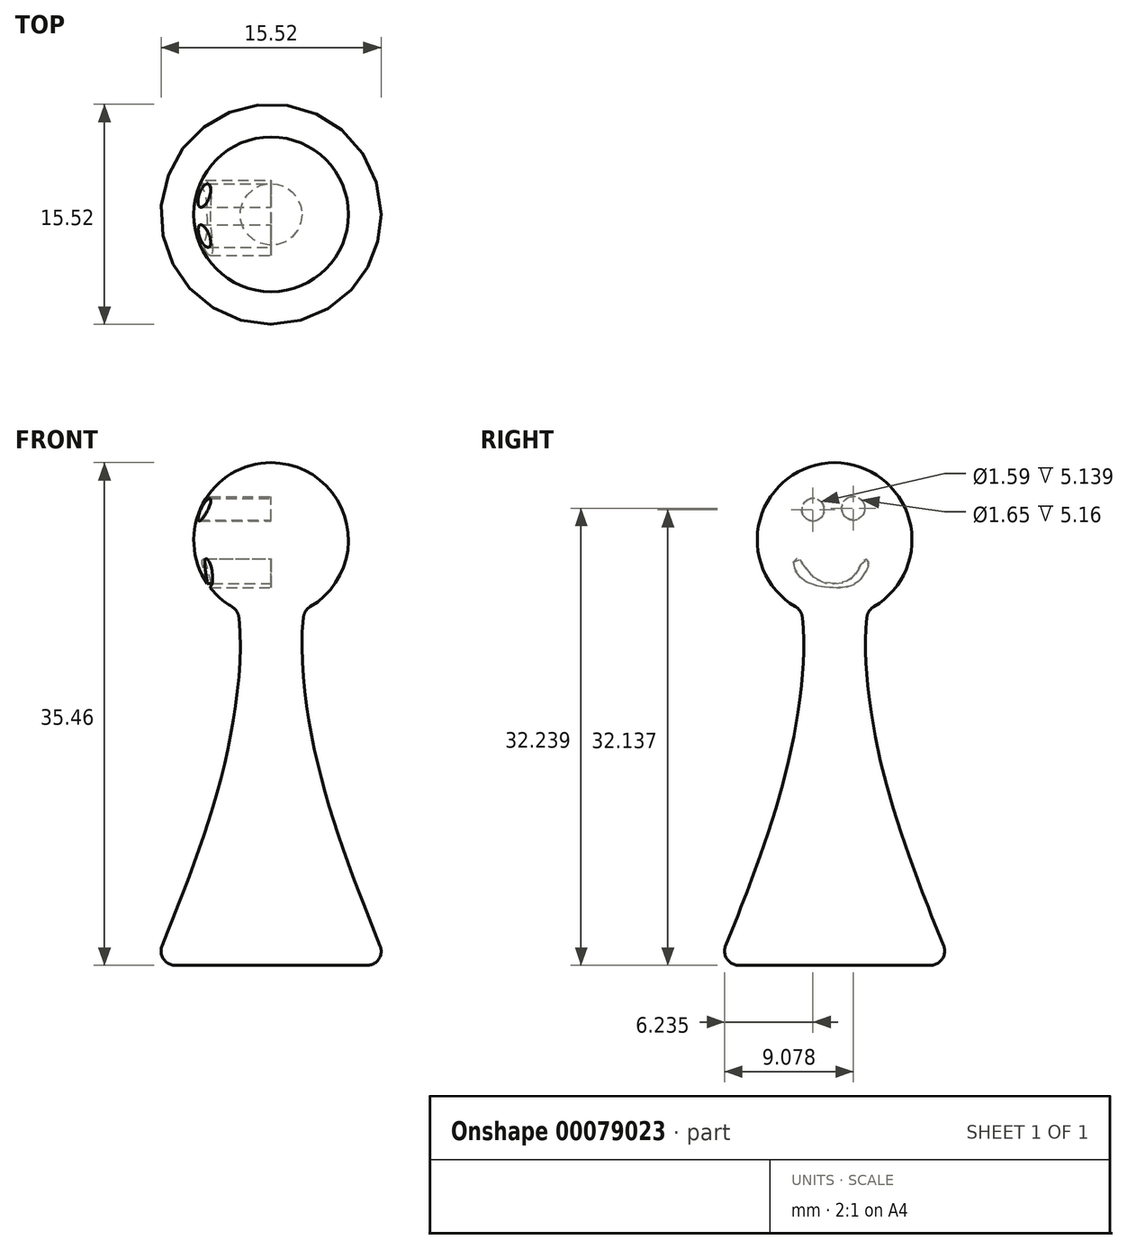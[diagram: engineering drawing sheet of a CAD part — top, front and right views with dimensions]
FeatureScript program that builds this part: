
annotation { "Feature Type Name" : "Feature", "Feature Type Description" : "" }
export const myFeature = defineFeature(function(context is Context, id is Id, definition is map)
    precondition{}
    {
        {
            var Q0;
            Q0=qCreatedBy(makeId("Front.planeOp"),FACE);
            var sketch = newSketch(context, id + "F0", { "sketchPlane" : qUnion([Q0])});
            skCircle(sketch, "E0", {"center": v(0, 0) * mm, "radius": 5.46 * mm});
            skLineSegment(sketch, "E1", {"start": v(0, 5.46) * mm, "end": v(0, -5.46) * mm});
            skSolve(sketch);
        }
        {
            var Q0;
            {var subQ0=sQuery(id+"F0.wireOp",EDGE,"E1");Q0=makeQuery(id+"F0.imprint","IMPRINT",FACE,{"disambiguationData":[TD([[makeQuery(id+"F0.imprint","IMPRINT",EDGE,{"derivedFrom":subQ0}),-1.0]])]});}
            var Q1;
            Q1=sQuery(id+"F0.wireOp",EDGE,"E1");
            revolve(context, id + "F1", {"entities" : qUnion([Q0]), "axis" : qUnion([Q1]), "revolveType" : RevolveType.FULL});
        }
        {
            var Q0;
            Q0=qCreatedBy(makeId("Top.planeOp"),FACE);
            var sketch = newSketch(context, id + "F2", { "sketchPlane" : qUnion([Q0])});
            skCircle(sketch, "E2", {"center": v(0, 0) * mm, "radius": 3.58 * mm});
            skSolve(sketch);
        }
        {
            var Q0;
            Q0=qCreatedBy(makeId("Top.planeOp"),FACE);
            cPlane(context, id + "F3", {"entities" : qUnion([Q0]), "cplaneType" : CPlaneType.OFFSET, "offset" : 5 * mm, "oppositeDirection" : true, "width" : 150 * mm, "height" : 150 * mm});
        }
        {
            var Q0;
            Q0=qCreatedBy(id+"F3.planeOp",FACE);
            var sketch = newSketch(context, id + "F4", { "sketchPlane" : qUnion([Q0])});
            skCircle(sketch, "E3", {"center": v(0, 0) * mm, "radius": 2.33 * mm});
            skSolve(sketch);
        }
        {
            var Q0;
            Q0=qCreatedBy(id+"F3.planeOp",FACE);
            cPlane(context, id + "F5", {"entities" : qUnion([Q0]), "cplaneType" : CPlaneType.OFFSET, "offset" : 5 * mm, "oppositeDirection" : true, "width" : 150 * mm, "height" : 150 * mm});
        }
        {
            var Q0;
            Q0=qCreatedBy(id+"F5.planeOp",FACE);
            var sketch = newSketch(context, id + "F6", { "sketchPlane" : qUnion([Q0])});
            skCircle(sketch, "E4", {"center": v(0, 0) * mm, "radius": 2.3 * mm});
            skSolve(sketch);
        }
        {
            var Q0;
            Q0=qCreatedBy(id+"F5.planeOp",FACE);
            cPlane(context, id + "F7", {"entities" : qUnion([Q0]), "cplaneType" : CPlaneType.OFFSET, "offset" : 20 * mm, "oppositeDirection" : true, "width" : 150 * mm, "height" : 150 * mm});
        }
        {
            var Q0;
            Q0=qCreatedBy(id+"F7.planeOp",FACE);
            var sketch = newSketch(context, id + "F8", { "sketchPlane" : qUnion([Q0])});
            skCircle(sketch, "E5", {"center": v(0, 0) * mm, "radius": 8.25 * mm});
            skSolve(sketch);
        }
        {
            var Q1;
            Q1 = qSketchRegion(id + "F8", true);
            var Q2;
            Q2 = qSketchRegion(id + "F6", true);
            var Q3;
            Q3 = qSketchRegion(id + "F4", true);
            var Q4;
            Q4 = qSketchRegion(id + "F2", true);
            loft(context, id + "F9", {"operationType" : NewBodyOperationType.ADD, "sheetProfilesArray" : [{ "sheetProfileEntities" : qUnion([Q1]) }, { "sheetProfileEntities" : qUnion([Q2]) }, { "sheetProfileEntities" : qUnion([Q3]) }, { "sheetProfileEntities" : qUnion([Q4]) }]});
        }
        {
            var Q0;
            Q0=qCreatedBy(makeId("Right.planeOp"),FACE);
            var sketch = newSketch(context, id + "F10", { "sketchPlane" : qUnion([Q0])});
            skCircle(sketch, "E6", {"center": v(-1.52, 2.14) * mm, "radius": 0.8 * mm});
            skCircle(sketch, "E7", {"center": v(1.32, 2.24) * mm, "radius": 0.83 * mm});
            skFitSpline(sketch, "E8", {"points": [v(-2.9, -1.54) * mm, v(-2.25, -2.78) * mm, v(0, -3.36) * mm, v(1.76, -2.87) * mm, v(2.39, -1.43) * mm, v(2.03, -1.42) * mm, v(1.32, -2.62) * mm, v(-1.29, -2.76) * mm, v(-2.56, -1.33) * mm, v(-2.9, -1.54) * mm]});
            skSolve(sketch);
        }
        {
            var Q0;
            Q0 = qSketchRegion(id + "F10", true);
            extrude(context, id + "F11", {"entities" : qUnion([Q0]), "operationType" : NewBodyOperationType.REMOVE, "oppositeDirection" : true, "depth" : 25 * mm});
        }
        {
            var Q0;
            Q0=makeQuery(id+"F9.opLoft","SWEPT_FACE",FACE,{"disambiguationData":[OSD([sQuery(id+"F6.wireOp",EDGE,"E4"),sQuery(id+"F8.wireOp",EDGE,"E5")])]});
            fillet(context, id + "F12", {"entities" : qUnion([Q0]), "radius" : 1 * mm, "tangentPropagation" : true, "allowEdgeOverflow" : false});
        }
    });
